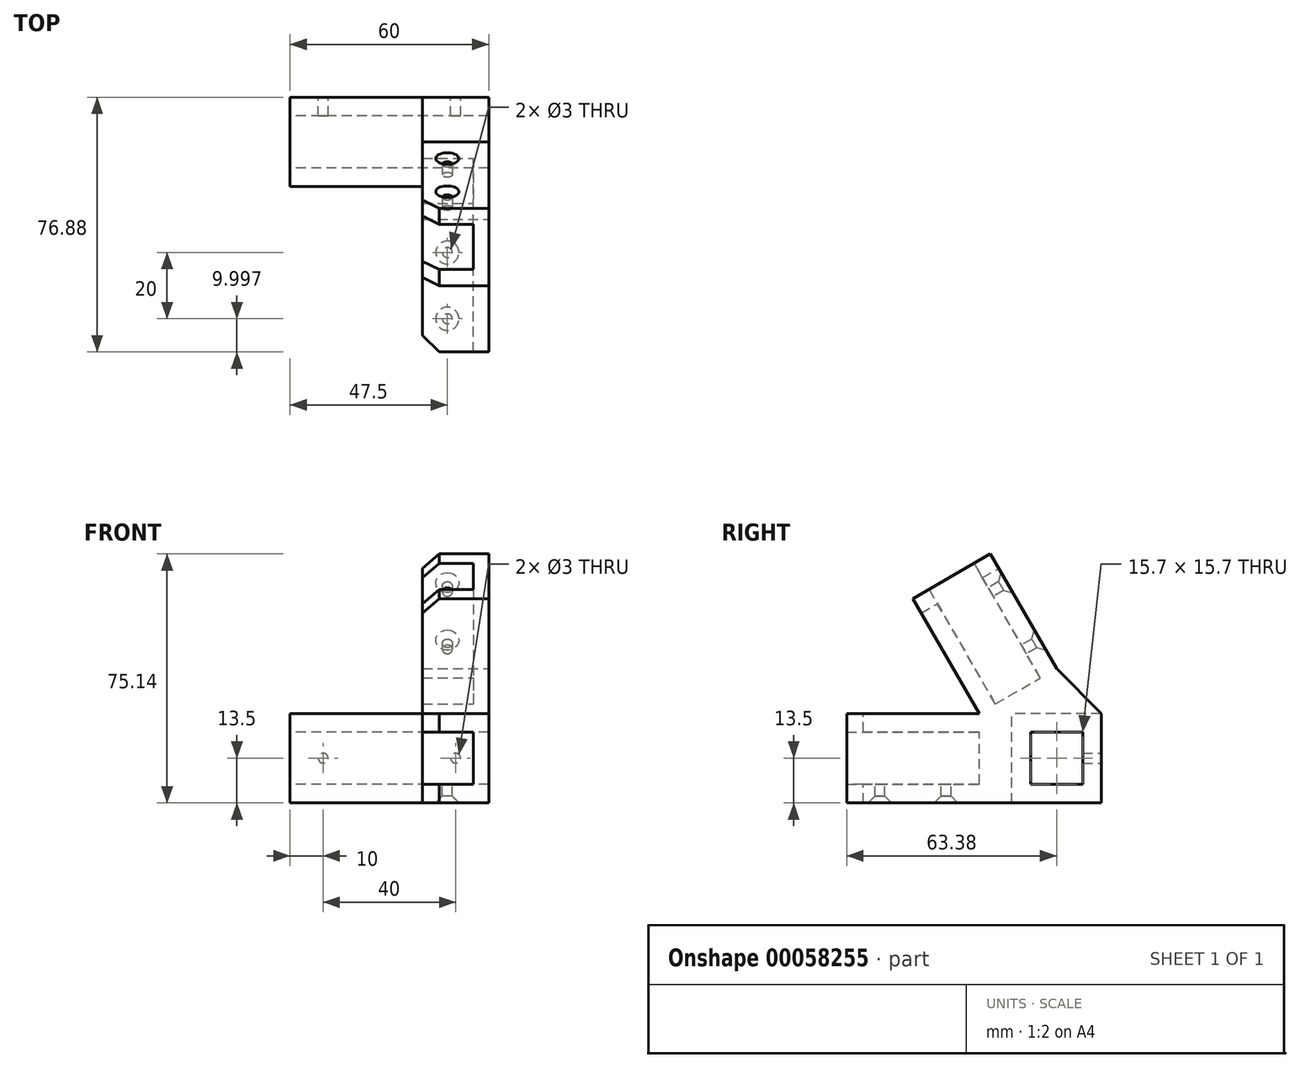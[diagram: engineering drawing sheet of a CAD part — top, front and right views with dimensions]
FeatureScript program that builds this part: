
annotation { "Feature Type Name" : "Feature", "Feature Type Description" : "" }
export const myFeature = defineFeature(function(context is Context, id is Id, definition is map)
    precondition{}
    {
        {
            var Q0;
            Q0=qCreatedBy(makeId("Right.planeOp"),FACE);
            var sketch = newSketch(context, id + "F0", { "sketchPlane" : qUnion([Q0])});
            skLineSegment(sketch, "E0", {"start": v(0, 0) * mm, "end": v(-49.64, 0) * mm, "construction": true});
            skLineSegment(sketch, "E1", {"start": v(0, 0) * mm, "end": v(-24.82, 43) * mm, "construction": true});
            skLineSegment(sketch, "E2", {"start": v(-24.82, 43) * mm, "end": v(-49.64, 0) * mm, "construction": true});
            skLineSegment(sketch, "E3", {"start": v(-37.23, 21.5) * mm, "end": v(0, 0) * mm, "construction": true});
            skLineSegment(sketch, "E4.bottom", {"start": v(7.5, 7.5) * mm, "end": v(-7.5, 7.5) * mm});
            skLineSegment(sketch, "E4.top", {"start": v(7.5, -7.5) * mm, "end": v(-7.5, -7.5) * mm});
            skLineSegment(sketch, "E4.left", {"start": v(7.5, 7.5) * mm, "end": v(7.5, -7.5) * mm});
            skLineSegment(sketch, "E4.right", {"start": v(-7.5, 7.5) * mm, "end": v(-7.5, -7.5) * mm});
            skPoint(sketch, "E4.middle", {"position": v(0, 0) * mm});
            skLineSegment(sketch, "E5", {"start": v(13.5, -13.5) * mm, "end": v(-63.38, -13.5) * mm});
            skLineSegment(sketch, "E6", {"start": v(13.5, -13.5) * mm, "end": v(13.5, 3.62) * mm});
            skLineSegment(sketch, "E7", {"start": v(13.5, 3.62) * mm, "end": v(-20, 61.64) * mm});
            skLineSegment(sketch, "E8", {"start": v(-23.38, 13.5) * mm, "end": v(-63.38, 13.5) * mm});
            skLineSegment(sketch, "E9", {"start": v(-23.38, 13.5) * mm, "end": v(-43.38, 48.14) * mm});
            skLineSegment(sketch, "E10", {"start": v(-43.38, 48.14) * mm, "end": v(-20, 61.64) * mm});
            skLineSegment(sketch, "E11", {"start": v(-63.38, 13.5) * mm, "end": v(-63.38, -13.5) * mm});
            skPoint(sketch, "E12", {"position": v(-23.38, 0) * mm});
            skSolve(sketch);
        }
        {
            var Q0;
            Q0 = qSketchRegion(id + "F0", true);
            extrude(context, id + "F1", {"entities" : qUnion([Q0]), "oppositeDirection" : true, "depth" : 20 * mm});
        }
        {
            var Q0;
            Q0=makeQuery(id+"F1.opExtrude","CAP_FACE",FACE,{"disambiguationData":[OSD([sQuery(id+"F0.wireOp",EDGE,"E4.bottom"),sQuery(id+"F0.wireOp",EDGE,"E4.top"),sQuery(id+"F0.wireOp",EDGE,"E4.left"),sQuery(id+"F0.wireOp",EDGE,"E4.right"),sQuery(id+"F0.wireOp",EDGE,"E5"),sQuery(id+"F0.wireOp",EDGE,"E6"),sQuery(id+"F0.wireOp",EDGE,"E7"),sQuery(id+"F0.wireOp",EDGE,"E8"),sQuery(id+"F0.wireOp",EDGE,"E9"),sQuery(id+"F0.wireOp",EDGE,"E10"),sQuery(id+"F0.wireOp",EDGE,"E11")])],"isStart":false});
            var sketch = newSketch(context, id + "F2", { "sketchPlane" : qUnion([Q0])});
            skLineSegment(sketch, "E13", {"start": v(23.38, 13.5) * mm, "end": v(0, 27) * mm, "construction": true});
            skLineSegment(sketch, "E14", {"start": v(11.7, 20.25) * mm, "end": v(31.7, 54.9) * mm, "construction": true});
            skLineSegment(sketch, "E15", {"start": v(18.19, 16.5) * mm, "end": v(38.19, 51.14) * mm});
            skLineSegment(sketch, "E16.MirrorCS", {"start": v(5.2, 24) * mm, "end": v(25.2, 58.64) * mm});
            skLineSegment(sketch, "E17", {"start": v(18.19, 16.5) * mm, "end": v(5.2, 24) * mm});
            skLineSegment(sketch, "E18", {"start": v(38.19, 51.14) * mm, "end": v(25.2, 58.64) * mm});
            skLineSegment(sketch, "E19.bottom", {"start": v(63.38, -7.5) * mm, "end": v(23.38, -7.5) * mm});
            skLineSegment(sketch, "E19.top", {"start": v(63.38, 7.5) * mm, "end": v(23.38, 7.5) * mm});
            skLineSegment(sketch, "E19.left", {"start": v(63.38, -7.5) * mm, "end": v(63.38, 7.5) * mm});
            skLineSegment(sketch, "E19.right", {"start": v(23.38, -7.5) * mm, "end": v(23.38, 7.5) * mm});
            skLineSegment(sketch, "E20", {"start": v(23.38, 0) * mm, "end": v(0, 0) * mm, "construction": true});
            skSolve(sketch);
        }
        {
            var Q0;
            Q0 = qSketchRegion(id + "F2", true);
            extrude(context, id + "F3", {"entities" : qUnion([Q0]), "operationType" : NewBodyOperationType.REMOVE, "oppositeDirection" : true, "depth" : 15 * mm});
        }
        {
            var Q0;
            Q0=makeQuery(id+"F1.opExtrude","CAP_FACE",FACE,{"disambiguationData":[OSD([sQuery(id+"F0.wireOp",EDGE,"E4.bottom"),sQuery(id+"F0.wireOp",EDGE,"E4.top"),sQuery(id+"F0.wireOp",EDGE,"E4.left"),sQuery(id+"F0.wireOp",EDGE,"E4.right"),sQuery(id+"F0.wireOp",EDGE,"E5"),sQuery(id+"F0.wireOp",EDGE,"E6"),sQuery(id+"F0.wireOp",EDGE,"E7"),sQuery(id+"F0.wireOp",EDGE,"E8"),sQuery(id+"F0.wireOp",EDGE,"E9"),sQuery(id+"F0.wireOp",EDGE,"E10"),sQuery(id+"F0.wireOp",EDGE,"E11")])],"isStart":true});
            var sketch = newSketch(context, id + "F4", { "sketchPlane" : qUnion([Q0])});
            skLineSegment(sketch, "E21.bottom", {"start": v(13.5, -13.5) * mm, "end": v(-13.5, -13.5) * mm});
            skLineSegment(sketch, "E21.top", {"start": v(13.5, 13.5) * mm, "end": v(-13.5, 13.5) * mm});
            skLineSegment(sketch, "E21.left", {"start": v(13.5, -13.5) * mm, "end": v(13.5, 13.5) * mm});
            skLineSegment(sketch, "E21.right", {"start": v(-13.5, -13.5) * mm, "end": v(-13.5, 13.5) * mm});
            skPoint(sketch, "E21.middle", {"position": v(0, 0) * mm});
            skLineSegment(sketch, "E22.bottom", {"start": v(7.5, 7.5) * mm, "end": v(-7.5, 7.5) * mm});
            skLineSegment(sketch, "E22.top", {"start": v(7.5, -7.5) * mm, "end": v(-7.5, -7.5) * mm});
            skLineSegment(sketch, "E22.left", {"start": v(7.5, 7.5) * mm, "end": v(7.5, -7.5) * mm});
            skLineSegment(sketch, "E22.right", {"start": v(-7.5, 7.5) * mm, "end": v(-7.5, -7.5) * mm});
            skSolve(sketch);
        }
        {
            var Q0;
            Q0 = qSketchRegion(id + "F4", true);
            extrude(context, id + "F5", {"entities" : qUnion([Q0]), "operationType" : NewBodyOperationType.ADD, "oppositeDirection" : true, "depth" : 60 * mm});
        }
        {
            var Q0;
            Q0=makeQuery(id+"F5.opExtrude","CAP_FACE",FACE,{"disambiguationData":[OSD([sQuery(id+"F4.wireOp",EDGE,"E21.bottom"),sQuery(id+"F4.wireOp",EDGE,"E21.top"),sQuery(id+"F4.wireOp",EDGE,"E21.left"),sQuery(id+"F4.wireOp",EDGE,"E21.right"),sQuery(id+"F4.wireOp",EDGE,"E22.bottom"),sQuery(id+"F4.wireOp",EDGE,"E22.top"),sQuery(id+"F4.wireOp",EDGE,"E22.left"),sQuery(id+"F4.wireOp",EDGE,"E22.right")])],"isStart":false});
            var sketch = newSketch(context, id + "F6", { "sketchPlane" : qUnion([Q0])});
            skLineSegment(sketch, "E23.bottom", {"start": v(7.85, 7.85) * mm, "end": v(-7.85, 7.85) * mm});
            skLineSegment(sketch, "E23.top", {"start": v(7.85, -7.85) * mm, "end": v(-7.85, -7.85) * mm});
            skLineSegment(sketch, "E23.left", {"start": v(7.85, 7.85) * mm, "end": v(7.85, -7.85) * mm});
            skLineSegment(sketch, "E23.right", {"start": v(-7.85, 7.85) * mm, "end": v(-7.85, -7.85) * mm});
            skPoint(sketch, "E23.middle", {"position": v(0, 0) * mm});
            skSolve(sketch);
        }
        {
            var Q0;
            Q0 = qSketchRegion(id + "F6", true);
            extrude(context, id + "F7", {"entities" : qUnion([Q0]), "operationType" : NewBodyOperationType.REMOVE, "endBound" : BoundingType.THROUGH_ALL, "oppositeDirection" : true, "depth" : 25 * mm});
        }
        {
            var Q0;
            Q0=makeQuery(id+"F3.boolean.opBoolean","COPY",FACE,{"derivedFrom":makeQuery(id+"F3.opExtrude","SWEPT_FACE",FACE,{"disambiguationData":[OSD([sQuery(id+"F2.wireOp",EDGE,"E19.right")])]})});
            var sketch = newSketch(context, id + "F8", { "sketchPlane" : qUnion([Q0])});
            skLineSegment(sketch, "E24", {"start": v(-20, 7.5) * mm, "end": v(-5, -7.5) * mm, "construction": true});
            skLineSegment(sketch, "E25.bottom", {"start": v(-20.35, 7.85) * mm, "end": v(-4.65, 7.85) * mm});
            skLineSegment(sketch, "E25.top", {"start": v(-20.35, -7.85) * mm, "end": v(-4.65, -7.85) * mm});
            skLineSegment(sketch, "E25.left", {"start": v(-20.35, 7.85) * mm, "end": v(-20.35, -7.85) * mm});
            skLineSegment(sketch, "E25.right", {"start": v(-4.65, 7.85) * mm, "end": v(-4.65, -7.85) * mm});
            skPoint(sketch, "E25.middle", {"position": v(-12.5, 0) * mm});
            skSolve(sketch);
        }
        {
            var Q0;
            Q0 = qSketchRegion(id + "F8", true);
            extrude(context, id + "F9", {"entities" : qUnion([Q0]), "operationType" : NewBodyOperationType.REMOVE, "endBound" : BoundingType.THROUGH_ALL, "depth" : 25 * mm});
        }
        {
            var Q0;
            Q0=makeQuery(id+"F3.boolean.opBoolean","COPY",FACE,{"derivedFrom":makeQuery(id+"F3.opExtrude","SWEPT_FACE",FACE,{"disambiguationData":[OSD([sQuery(id+"F2.wireOp",EDGE,"E17")])]})});
            var sketch = newSketch(context, id + "F10", { "sketchPlane" : qUnion([Q0])});
            skLineSegment(sketch, "E26", {"start": v(-20, 7.5) * mm, "end": v(-5, -7.5) * mm, "construction": true});
            skLineSegment(sketch, "E27.bottom", {"start": v(-20.35, 7.85) * mm, "end": v(-4.65, 7.85) * mm});
            skLineSegment(sketch, "E27.top", {"start": v(-20.35, -7.85) * mm, "end": v(-4.65, -7.85) * mm});
            skLineSegment(sketch, "E27.left", {"start": v(-20.35, 7.85) * mm, "end": v(-20.35, -7.85) * mm});
            skLineSegment(sketch, "E27.right", {"start": v(-4.65, 7.85) * mm, "end": v(-4.65, -7.85) * mm});
            skPoint(sketch, "E27.middle", {"position": v(-12.5, 0) * mm});
            skSolve(sketch);
        }
        {
            var Q0;
            Q0 = qSketchRegion(id + "F10", true);
            extrude(context, id + "F11", {"entities" : qUnion([Q0]), "operationType" : NewBodyOperationType.REMOVE, "endBound" : BoundingType.THROUGH_ALL, "depth" : 25 * mm});
        }
        {
            var Q0;
            Q0=makeQuery(id+"F5.boolean.opBoolean","MERGE",FACE,{"derivedFrom":[makeQuery(id+"F1.opExtrude","SWEPT_FACE",FACE,{"disambiguationData":[OSD([sQuery(id+"F0.wireOp",EDGE,"E6")])]}),makeQuery(id+"F5.opExtrude","SWEPT_FACE",FACE,{"disambiguationData":[OSD([sQuery(id+"F4.wireOp",EDGE,"E21.left")])]})]});
            var sketch = newSketch(context, id + "F12", { "sketchPlane" : qUnion([Q0])});
            skLineSegment(sketch, "E28", {"start": v(0, 0) * mm, "end": v(60, 0) * mm, "construction": true});
            skCircle(sketch, "E29", {"center": v(10, 0) * mm, "radius": 1.5 * mm});
            skCircle(sketch, "E30", {"center": v(50, 0) * mm, "radius": 1.5 * mm});
            skSolve(sketch);
        }
        {
            var Q0;
            Q0 = qSketchRegion(id + "F12", true);
            extrude(context, id + "F13", {"entities" : qUnion([Q0]), "operationType" : NewBodyOperationType.REMOVE, "endBound" : BoundingType.UP_TO_NEXT, "oppositeDirection" : true, "depth" : 25 * mm});
        }
        {
            var Q0;
            Q0=makeQuery(id+"F11.boolean.opBoolean","COPY",FACE,{"derivedFrom":makeQuery(id+"F11.opExtrude","SWEPT_FACE",FACE,{"disambiguationData":[OSD([sQuery(id+"F10.wireOp",EDGE,"E27.bottom")])]})});
            var sketch = newSketch(context, id + "F14", { "sketchPlane" : qUnion([Q0])});
            skLineSegment(sketch, "E31", {"start": v(-12.5, 23.38) * mm, "end": v(-12.5, 63.38) * mm, "construction": true});
            skCircle(sketch, "E32", {"center": v(-12.5, 33.38) * mm, "radius": 1.5 * mm});
            skCircle(sketch, "E33", {"center": v(-12.5, 53.38) * mm, "radius": 1.5 * mm});
            skSolve(sketch);
        }
        {
            var Q0;
            Q0 = qSketchRegion(id + "F14", true);
            extrude(context, id + "F15", {"entities" : qUnion([Q0]), "operationType" : NewBodyOperationType.REMOVE, "endBound" : BoundingType.THROUGH_ALL, "oppositeDirection" : true, "depth" : 25 * mm});
        }
        {
            var Q0;
            Q0=makeQuery(id+"F9.boolean.opBoolean","COPY",FACE,{"derivedFrom":makeQuery(id+"F9.opExtrude","SWEPT_FACE",FACE,{"disambiguationData":[OSD([sQuery(id+"F8.wireOp",EDGE,"E25.top")])]})});
            var sketch = newSketch(context, id + "F16", { "sketchPlane" : qUnion([Q0])});
            skLineSegment(sketch, "E34", {"start": v(-12.5, -23.38) * mm, "end": v(-12.5, -63.38) * mm, "construction": true});
            skCircle(sketch, "E35", {"center": v(-12.5, -53.38) * mm, "radius": 1.5 * mm});
            skCircle(sketch, "E36", {"center": v(-12.5, -33.38) * mm, "radius": 1.5 * mm});
            skSolve(sketch);
        }
        {
            var Q0;
            Q0 = qSketchRegion(id + "F16", true);
            extrude(context, id + "F17", {"entities" : qUnion([Q0]), "operationType" : NewBodyOperationType.REMOVE, "endBound" : BoundingType.THROUGH_ALL, "oppositeDirection" : true, "depth" : 25 * mm});
        }
        {
            var Q0;
            {var subQ0=sQuery(id+"F0.wireOp",EDGE,"E10");var subQ1=sQuery(id+"F0.wireOp",EDGE,"E9");Q0=makeQuery(id+"F3.boolean.opBoolean","SPLIT",EDGE,{"disambiguationData":[TD([makeQuery(id+"F1.opExtrude","SWEPT_FACE",FACE,{"disambiguationData":[OSD([subQ1])]})])],"derivedFrom":makeQuery(id+"F1.opExtrude","CAP_EDGE",EDGE,{"disambiguationData":[OSD([subQ0])],"isStart":false})});}
            var Q1;
            {var subQ0=sQuery(id+"F0.wireOp",EDGE,"E10");var subQ1=sQuery(id+"F0.wireOp",EDGE,"E7");Q1=makeQuery(id+"F3.boolean.opBoolean","SPLIT",EDGE,{"disambiguationData":[TD([makeQuery(id+"F1.opExtrude","SWEPT_FACE",FACE,{"disambiguationData":[OSD([subQ1])]})])],"derivedFrom":makeQuery(id+"F1.opExtrude","CAP_EDGE",EDGE,{"disambiguationData":[OSD([subQ0])],"isStart":false})});}
            var Q2;
            {var subQ0=sQuery(id+"F0.wireOp",EDGE,"E11");var subQ1=sQuery(id+"F0.wireOp",EDGE,"E8");Q2=makeQuery(id+"F3.boolean.opBoolean","SPLIT",EDGE,{"disambiguationData":[TD([makeQuery(id+"F1.opExtrude","SWEPT_FACE",FACE,{"disambiguationData":[OSD([subQ1])]})])],"derivedFrom":makeQuery(id+"F1.opExtrude","CAP_EDGE",EDGE,{"disambiguationData":[OSD([subQ0])],"isStart":false})});}
            var Q3;
            {var subQ0=sQuery(id+"F0.wireOp",EDGE,"E11");var subQ1=sQuery(id+"F0.wireOp",EDGE,"E5");Q3=makeQuery(id+"F3.boolean.opBoolean","SPLIT",EDGE,{"disambiguationData":[TD([makeQuery(id+"F1.opExtrude","SWEPT_FACE",FACE,{"disambiguationData":[OSD([subQ1])]})])],"derivedFrom":makeQuery(id+"F1.opExtrude","CAP_EDGE",EDGE,{"disambiguationData":[OSD([subQ0])],"isStart":false})});}
            chamfer(context, id + "F18", {"entities" : qUnion([Q0, Q1, Q2, Q3]), "width" : 5 * mm, "tangentPropagation" : true});
        }
        {
            var Q0;
            Q0=makeQuery(id+"F15.boolean.opBoolean","INTERSECT",EDGE,{"derivedFrom":[makeQuery(id+"F1.opExtrude","SWEPT_FACE",FACE,{"disambiguationData":[OSD([sQuery(id+"F0.wireOp",EDGE,"E7")])]}),makeQuery(id+"F15.opExtrude","SWEPT_FACE",FACE,{"disambiguationData":[OSD([sQuery(id+"F14.wireOp",EDGE,"E33")])]})]});
            var Q1;
            Q1=makeQuery(id+"F15.boolean.opBoolean","INTERSECT",EDGE,{"derivedFrom":[makeQuery(id+"F1.opExtrude","SWEPT_FACE",FACE,{"disambiguationData":[OSD([sQuery(id+"F0.wireOp",EDGE,"E7")])]}),makeQuery(id+"F15.opExtrude","SWEPT_FACE",FACE,{"disambiguationData":[OSD([sQuery(id+"F14.wireOp",EDGE,"E32")])]})]});
            var Q2;
            Q2=makeQuery(id+"F13.boolean.opBoolean","COPY",EDGE,{"derivedFrom":makeQuery(id+"F13.opExtrude","CAP_EDGE",EDGE,{"disambiguationData":[OSD([sQuery(id+"F12.wireOp",EDGE,"E29")])],"isStart":true})});
            var Q3;
            Q3=makeQuery(id+"F13.boolean.opBoolean","COPY",EDGE,{"derivedFrom":makeQuery(id+"F13.opExtrude","CAP_EDGE",EDGE,{"disambiguationData":[OSD([sQuery(id+"F12.wireOp",EDGE,"E30")])],"isStart":true})});
            var Q4;
            Q4=makeQuery(id+"F17.boolean.opBoolean","INTERSECT",EDGE,{"derivedFrom":[makeQuery(id+"F5.boolean.opBoolean","MERGE",FACE,{"derivedFrom":[makeQuery(id+"F1.opExtrude","SWEPT_FACE",FACE,{"disambiguationData":[OSD([sQuery(id+"F0.wireOp",EDGE,"E5")])]}),makeQuery(id+"F5.opExtrude","SWEPT_FACE",FACE,{"disambiguationData":[OSD([sQuery(id+"F4.wireOp",EDGE,"E21.bottom")])]})]}),makeQuery(id+"F17.opExtrude","SWEPT_FACE",FACE,{"disambiguationData":[OSD([sQuery(id+"F16.wireOp",EDGE,"E36")])]})]});
            var Q5;
            Q5=makeQuery(id+"F17.boolean.opBoolean","INTERSECT",EDGE,{"derivedFrom":[makeQuery(id+"F5.boolean.opBoolean","MERGE",FACE,{"derivedFrom":[makeQuery(id+"F1.opExtrude","SWEPT_FACE",FACE,{"disambiguationData":[OSD([sQuery(id+"F0.wireOp",EDGE,"E5")])]}),makeQuery(id+"F5.opExtrude","SWEPT_FACE",FACE,{"disambiguationData":[OSD([sQuery(id+"F4.wireOp",EDGE,"E21.bottom")])]})]}),makeQuery(id+"F17.opExtrude","SWEPT_FACE",FACE,{"disambiguationData":[OSD([sQuery(id+"F16.wireOp",EDGE,"E35")])]})]});
            chamfer(context, id + "F19", {"entities" : qUnion([Q0, Q1, Q2, Q3, Q4, Q5]), "width" : 2 * mm, "tangentPropagation" : true});
        }
        {
            var Q0;
            Q0=makeQuery(id+"F5.boolean.opBoolean","MERGE",FACE,{"derivedFrom":[makeQuery(id+"F1.opExtrude","CAP_FACE",FACE,{"disambiguationData":[OSD([sQuery(id+"F0.wireOp",EDGE,"E4.bottom"),sQuery(id+"F0.wireOp",EDGE,"E4.top"),sQuery(id+"F0.wireOp",EDGE,"E4.left"),sQuery(id+"F0.wireOp",EDGE,"E4.right"),sQuery(id+"F0.wireOp",EDGE,"E5"),sQuery(id+"F0.wireOp",EDGE,"E6"),sQuery(id+"F0.wireOp",EDGE,"E7"),sQuery(id+"F0.wireOp",EDGE,"E8"),sQuery(id+"F0.wireOp",EDGE,"E9"),sQuery(id+"F0.wireOp",EDGE,"E10"),sQuery(id+"F0.wireOp",EDGE,"E11")])],"isStart":true}),makeQuery(id+"F5.opExtrude","CAP_FACE",FACE,{"disambiguationData":[OSD([sQuery(id+"F4.wireOp",EDGE,"E21.bottom"),sQuery(id+"F4.wireOp",EDGE,"E21.top"),sQuery(id+"F4.wireOp",EDGE,"E21.left"),sQuery(id+"F4.wireOp",EDGE,"E21.right"),sQuery(id+"F4.wireOp",EDGE,"E22.bottom"),sQuery(id+"F4.wireOp",EDGE,"E22.top"),sQuery(id+"F4.wireOp",EDGE,"E22.left"),sQuery(id+"F4.wireOp",EDGE,"E22.right")])],"isStart":true})]});
            var sketch = newSketch(context, id + "F20", { "sketchPlane" : qUnion([Q0])});
            skLineSegment(sketch, "E37.0", {"start": v(13.5, 13.5) * mm, "end": v(7.8, 13.5) * mm});
            skLineSegment(sketch, "E38", {"start": v(13.5, 13.5) * mm, "end": v(0, 27) * mm});
            skLineSegment(sketch, "E39", {"start": v(0, 27) * mm, "end": v(7.8, 13.5) * mm});
            skSolve(sketch);
        }
        {
            var Q0;
            Q0 = qSketchRegion(id + "F20", true);
            var Q1;
            Q1=makeQuery(id+"F1.opExtrude","CAP_FACE",FACE,{"disambiguationData":[OSD([sQuery(id+"F0.wireOp",EDGE,"E4.bottom"),sQuery(id+"F0.wireOp",EDGE,"E4.top"),sQuery(id+"F0.wireOp",EDGE,"E4.left"),sQuery(id+"F0.wireOp",EDGE,"E4.right"),sQuery(id+"F0.wireOp",EDGE,"E5"),sQuery(id+"F0.wireOp",EDGE,"E6"),sQuery(id+"F0.wireOp",EDGE,"E7"),sQuery(id+"F0.wireOp",EDGE,"E8"),sQuery(id+"F0.wireOp",EDGE,"E9"),sQuery(id+"F0.wireOp",EDGE,"E10"),sQuery(id+"F0.wireOp",EDGE,"E11")])],"isStart":false});
            extrude(context, id + "F21", {"entities" : qUnion([Q0]), "operationType" : NewBodyOperationType.ADD, "endBound" : BoundingType.UP_TO_SURFACE, "oppositeDirection" : true, "endBoundEntityFace" : qUnion([Q1]), "depth" : 25 * mm});
        }
    });
